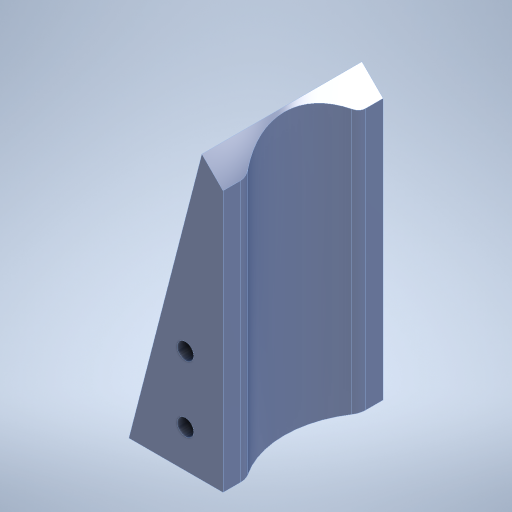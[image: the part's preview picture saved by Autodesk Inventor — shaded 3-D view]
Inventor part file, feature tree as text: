
AUTODESK INVENTOR PART (.ipt)
format: ipt  version: 2024.2 (Build 282272000, 272)  size: 292,352 bytes
history: native  units: mm
features: extrude x5, sketch x5, chamfer x1, shell x1, fillet x1, plane x1, mirror x1
ambient origin geometry x8: Origin, YZ Plane, XZ Plane, XY Plane, X Axis, Y Axis, Z Axis, Center Point
bodies: Solid1 (feature_tree)
feature tree (15):
  extrude  "Extrusion1"  Depth=20.0mm
  chamfer  "Chamfer1"  Distance=60.0mm
  extrude  "Extrusion2"  Depth=60.0mm TaperAngle=0.0deg
  extrude  "Extrusion7"  Depth=16.0mm
  shell  "Shell2"  Thickness=0.0mm
  extrude  "Extrusion8"  Depth=3.0mm
  fillet  "Fillet2"  Radius=4.5mm
  extrude  "Extrusion9"  Depth=10.0mm
  plane  "Work Plane1"
  mirror  "Mirror1"
  sketch  "Sketch1"  dims[d0=34.0mm d1=20.0mm d2=60.0mm d3=0.0mm]
  sketch  "Sketch3"  dims[d4=4.5mm d5=2.0mm d6=45.0deg d7=60.0mm d8=0.0mm]
  sketch  "Sketch8"  dims[d44=40.0mm d45=16.0mm d46=0.0mm d47=0.0mm]
  sketch  "Sketch9"  dims[d48=3.0mm d49=4.5mm d50=4.5mm]
  sketch  "Sketch10"  dims[d51=5.0mm d52=10.0mm d53=360.0deg d54=4.5mm d56=25.0mm d57=3.0mm d58=0.0mm d59=4.0mm d60=3.5mm d61=12.0mm d62=8.0mm d64=3.5mm d65=3.0mm d66=0.0mm d67=-17.0mm d17=0.5mm d18=0.872665mm d19=0.5mm d20=0.872665mm]
